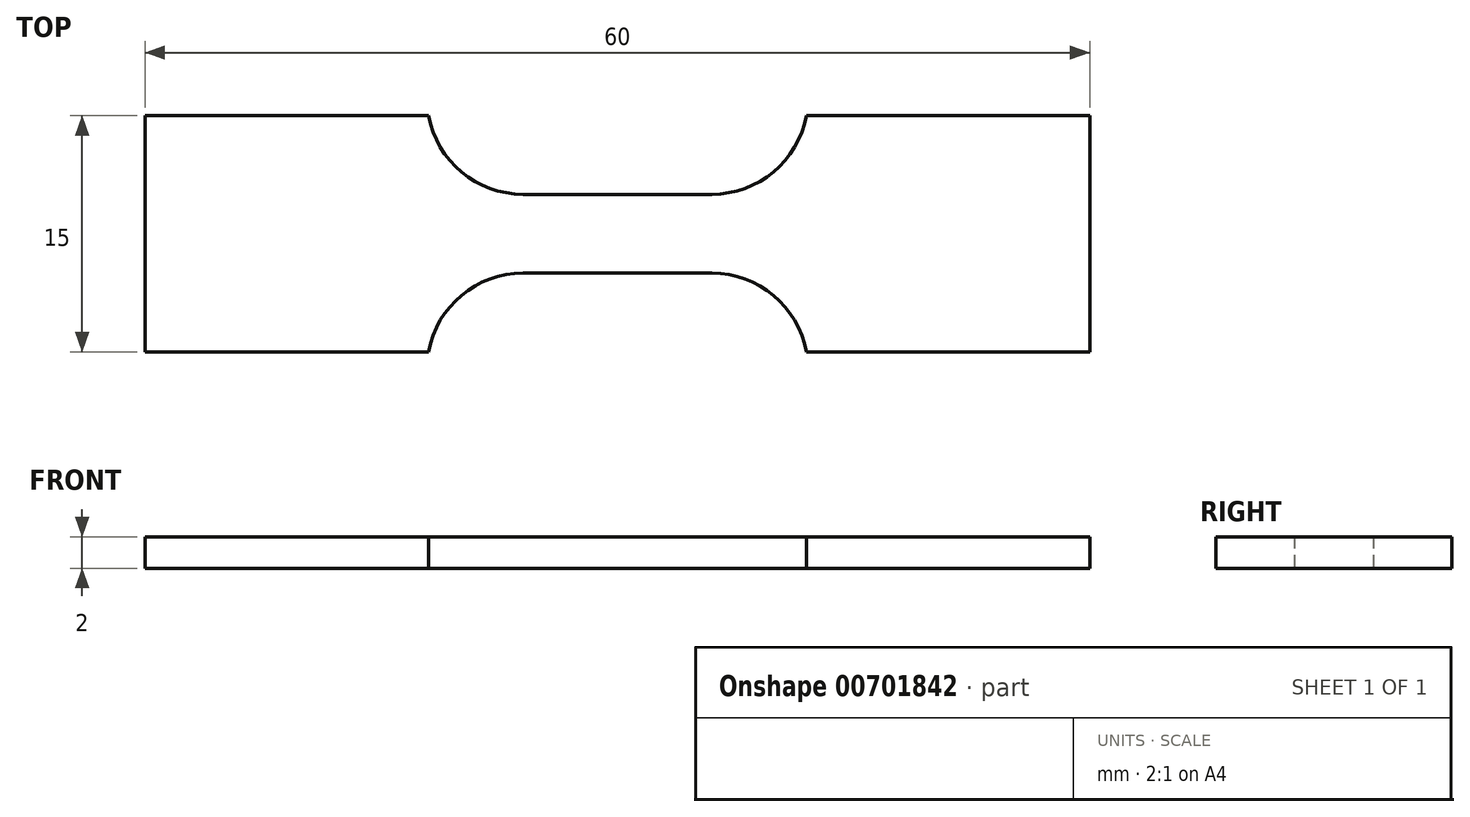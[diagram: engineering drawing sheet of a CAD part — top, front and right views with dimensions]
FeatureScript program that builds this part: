
annotation { "Feature Type Name" : "Feature", "Feature Type Description" : "" }
export const myFeature = defineFeature(function(context is Context, id is Id, definition is map)
    precondition{}
    {
        {
            var Q0;
            Q0=qCreatedBy(makeId("Top.planeOp"),FACE);
            var sketch = newSketch(context, id + "F0", { "sketchPlane" : qUnion([Q0])});
            skLineSegment(sketch, "E0", {"start": v(-15.16, 2.35) * mm, "end": v(-15.16, -5.15) * mm});
            skLineSegment(sketch, "E1", {"start": v(-15.16, -5.15) * mm, "end": v(2.84, -5.15) * mm});
            skArc(sketch, "E2", {"start": v(8.84, -0.15) * mm, "mid": v(4.93, -1.56) * mm, "end": v(2.84, -5.15) * mm});
            skLineSegment(sketch, "E3", {"start": v(8.84, -0.15) * mm, "end": v(20.84, -0.15) * mm});
            skArc(sketch, "E4", {"start": v(26.84, -5.15) * mm, "mid": v(24.74, -1.56) * mm, "end": v(20.84, -0.15) * mm});
            skLineSegment(sketch, "E5", {"start": v(26.84, -5.15) * mm, "end": v(44.84, -5.15) * mm});
            skLineSegment(sketch, "E6", {"start": v(44.84, -5.15) * mm, "end": v(44.84, 2.35) * mm});
            skPoint(sketch, "E7.start.orphan", {"position": v(44.84, 9.85) * mm});
            skPoint(sketch, "E8.MirrorCS.start.orphan", {"position": v(-11.16, 9.85) * mm});
            skPoint(sketch, "E9.end.orphan", {"position": v(-15.16, 9.85) * mm});
            skLineSegment(sketch, "E10.MirrorCS", {"start": v(8.84, 4.85) * mm, "end": v(20.84, 4.85) * mm});
            skArc(sketch, "E11.MirrorCS", {"start": v(26.84, 9.85) * mm, "mid": v(24.74, 6.27) * mm, "end": v(20.84, 4.85) * mm});
            skLineSegment(sketch, "E12.MirrorCS", {"start": v(-15.16, 2.35) * mm, "end": v(-15.16, 9.85) * mm});
            skLineSegment(sketch, "E13.MirrorCS", {"start": v(44.84, 9.85) * mm, "end": v(44.84, 2.35) * mm});
            skLineSegment(sketch, "E14.MirrorCS", {"start": v(-15.16, 9.85) * mm, "end": v(2.84, 9.85) * mm});
            skArc(sketch, "E15.MirrorCS", {"start": v(8.84, 4.85) * mm, "mid": v(4.93, 6.27) * mm, "end": v(2.84, 9.85) * mm});
            skLineSegment(sketch, "E16.MirrorCS", {"start": v(26.84, 9.85) * mm, "end": v(44.84, 9.85) * mm});
            skSolve(sketch);
        }
        {
            var Q0;
            Q0=makeQuery(id+"F0.imprint","IMPRINT",FACE,{"disambiguationData":[TD([[makeQuery(id+"F0.imprint","IMPRINT",EDGE,{"derivedFrom":sQuery(id+"F0.wireOp",EDGE,"E0")}),1.0]])]});
            extrude(context, id + "F1", {"entities" : qUnion([Q0]), "flatOperationType" : FlatOperationType.REMOVE, "depth" : 2 * mm, "offsetDistance" : 25 * mm, "domain" : OperationDomain.MODEL});
        }
    });
